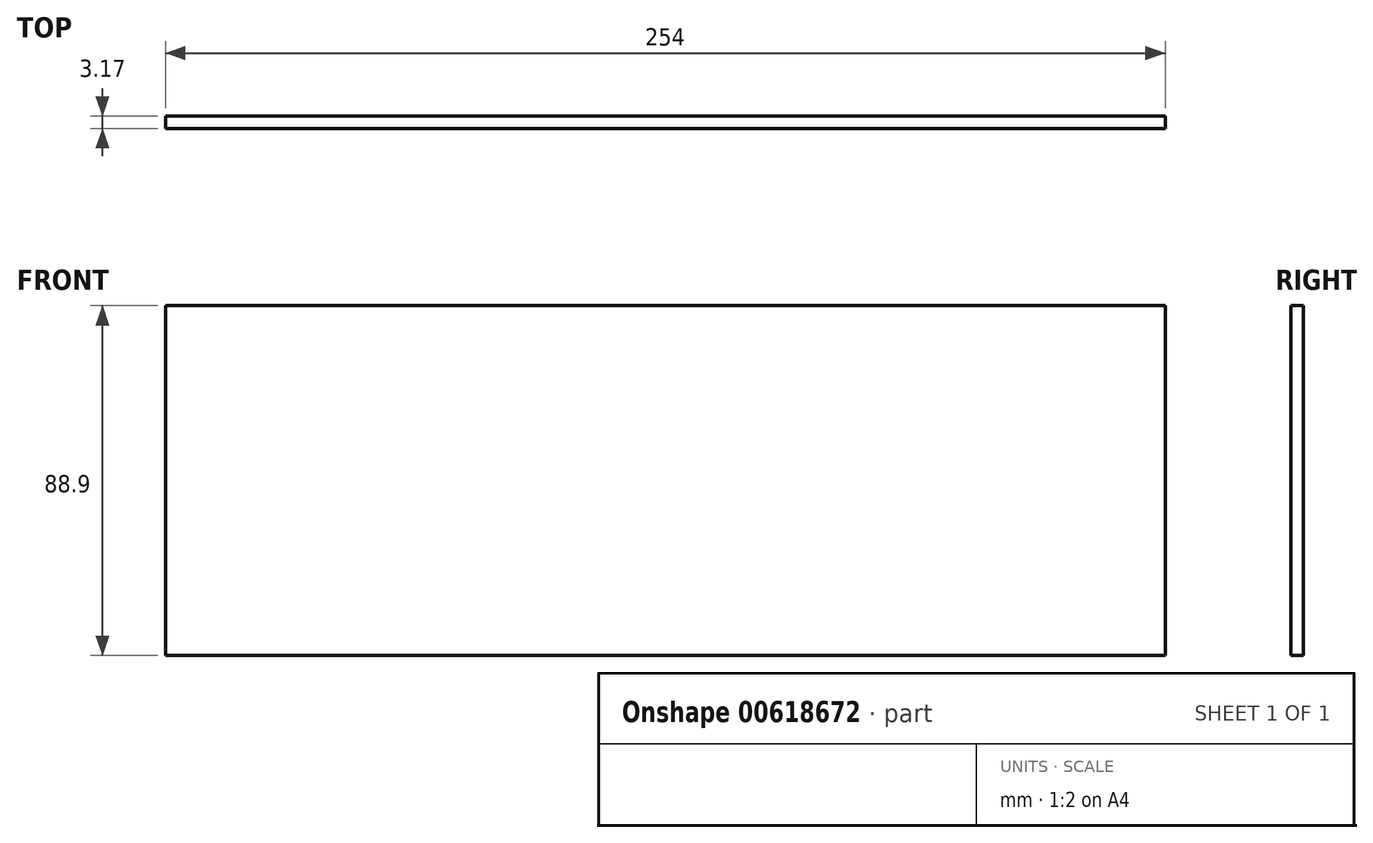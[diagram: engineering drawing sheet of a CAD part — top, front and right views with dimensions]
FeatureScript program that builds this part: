
annotation { "Feature Type Name" : "Feature", "Feature Type Description" : "" }
export const myFeature = defineFeature(function(context is Context, id is Id, definition is map)
    precondition{}
    {
        {
            var Q0;
            Q0=qCreatedBy(makeId("Front.planeOp"),FACE);
            var sketch = newSketch(context, id + "F0", { "sketchPlane" : qUnion([Q0])});
            skLineSegment(sketch, "E0.bottom", {"start": v(0, 0) * mm, "end": v(254, 0) * mm});
            skLineSegment(sketch, "E0.top", {"start": v(0, 88.9) * mm, "end": v(254, 88.9) * mm});
            skLineSegment(sketch, "E0.left", {"start": v(0, 0) * mm, "end": v(0, 88.9) * mm});
            skLineSegment(sketch, "E0.right", {"start": v(254, 0) * mm, "end": v(254, 88.9) * mm});
            skSolve(sketch);
        }
        {
            var Q0;
            Q0=makeQuery(id+"F0.imprint","IMPRINT",FACE,{"disambiguationData":[TD([[makeQuery(id+"F0.imprint","IMPRINT",EDGE,{"derivedFrom":sQuery(id+"F0.wireOp",EDGE,"E0.bottom")}),1.0]])]});
            extrude(context, id + "F1", {"entities" : qUnion([Q0]), "depth" : 3.17 * mm, "offsetDistance" : 25.4 * mm});
        }
    });
